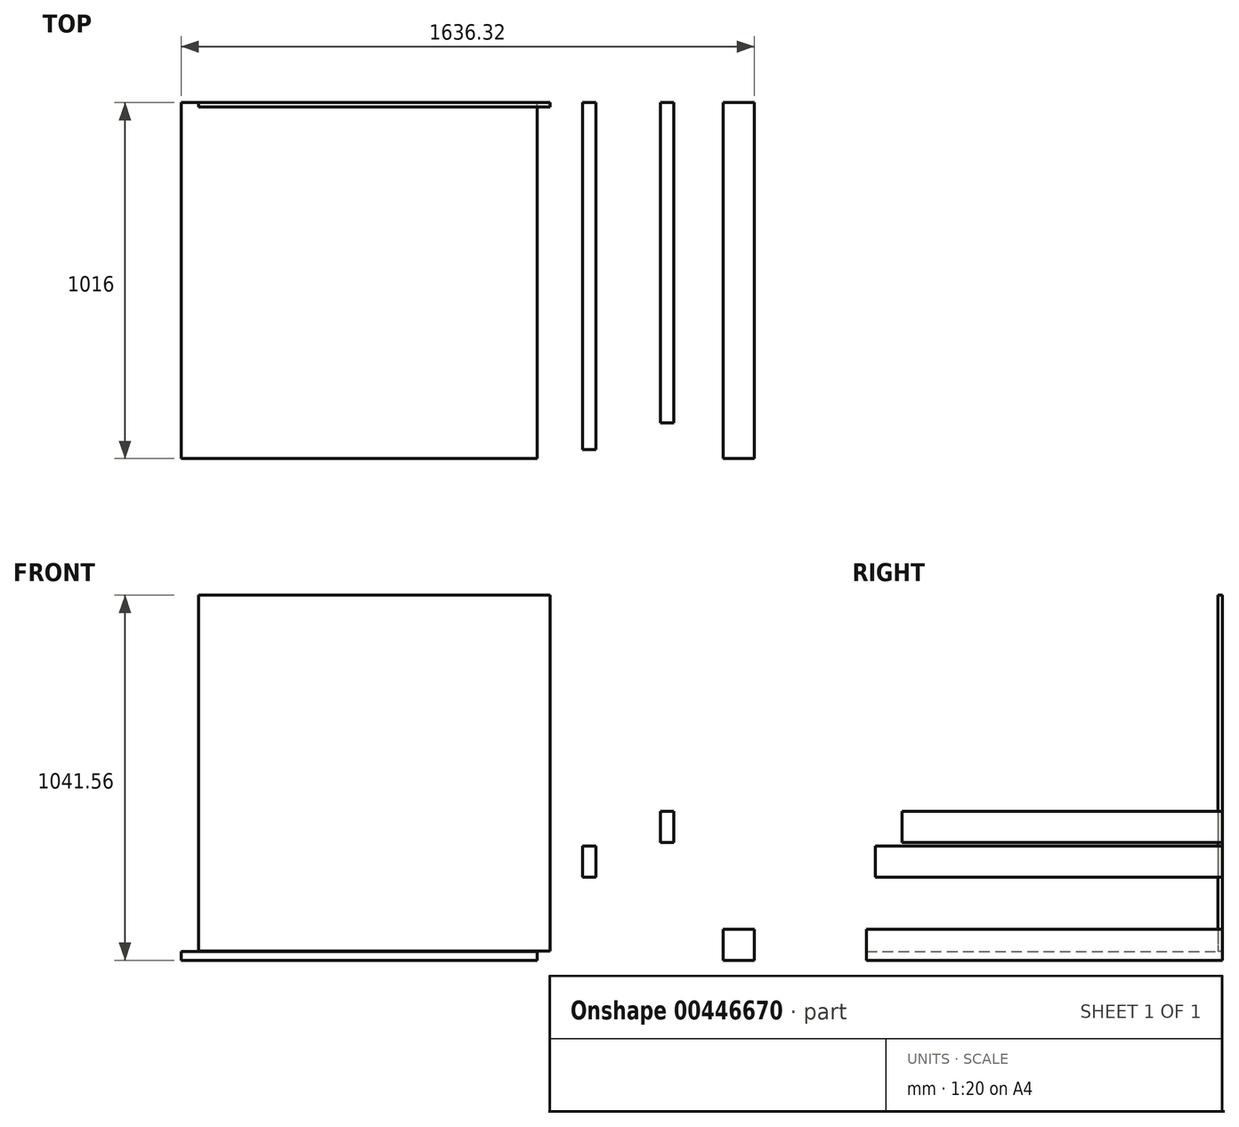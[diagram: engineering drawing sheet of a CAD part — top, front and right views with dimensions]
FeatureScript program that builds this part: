
annotation { "Feature Type Name" : "Feature", "Feature Type Description" : "" }
export const myFeature = defineFeature(function(context is Context, id is Id, definition is map)
    precondition{}
    {
        {
            var Q0;
            Q0=qCreatedBy(makeId("Front.planeOp"),FACE);
            var sketch = newSketch(context, id + "F0", { "sketchPlane" : qUnion([Q0])});
            skLineSegment(sketch, "E0.bottom", {"start": v(0, 0) * mm, "end": v(88.9, 0) * mm});
            skLineSegment(sketch, "E0.top", {"start": v(0, 88.9) * mm, "end": v(88.9, 88.9) * mm});
            skLineSegment(sketch, "E0.left", {"start": v(0, 0) * mm, "end": v(0, 88.9) * mm});
            skLineSegment(sketch, "E0.right", {"start": v(88.9, 0) * mm, "end": v(88.9, 88.9) * mm});
            skSolve(sketch);
        }
        {
            var Q0;
            Q0=makeQuery(id+"F0.imprint","IMPRINT",FACE,{"disambiguationData":[TD([[makeQuery(id+"F0.imprint","IMPRINT",EDGE,{"derivedFrom":sQuery(id+"F0.wireOp",EDGE,"E0.bottom")}),1.0]])]});
            extrude(context, id + "F1", {"entities" : qUnion([Q0]), "depth" : 1016 * mm, "offsetDistance" : 25.4 * mm});
        }
        {
            var Q0;
            Q0=qCreatedBy(makeId("Top.planeOp"),FACE);
            var sketch = newSketch(context, id + "F2", { "sketchPlane" : qUnion([Q0])});
            skLineSegment(sketch, "E1.bottom", {"start": v(-531.42, -1016) * mm, "end": v(-1547.42, -1016) * mm});
            skLineSegment(sketch, "E1.top", {"start": v(-531.42, 0) * mm, "end": v(-1547.42, 0) * mm});
            skLineSegment(sketch, "E1.left", {"start": v(-531.42, -1016) * mm, "end": v(-531.42, 0) * mm});
            skLineSegment(sketch, "E1.right", {"start": v(-1547.42, -1016) * mm, "end": v(-1547.42, 0) * mm});
            skSolve(sketch);
        }
        {
            var Q0;
            Q0=makeQuery(id+"F2.imprint","IMPRINT",FACE,{"disambiguationData":[TD([[makeQuery(id+"F2.imprint","IMPRINT",EDGE,{"derivedFrom":sQuery(id+"F2.wireOp",EDGE,"E1.bottom")}),-1.0]])]});
            extrude(context, id + "F3", {"entities" : qUnion([Q0]), "depth" : 25.4 * mm, "offsetDistance" : 25.4 * mm});
        }
        {
            var Q0;
            Q0=qCreatedBy(makeId("Front.planeOp"),FACE);
            var sketch = newSketch(context, id + "F4", { "sketchPlane" : qUnion([Q0])});
            skLineSegment(sketch, "E2.bottom", {"start": v(-401.15, 236.5) * mm, "end": v(-363.05, 236.5) * mm});
            skLineSegment(sketch, "E2.top", {"start": v(-401.15, 325.4) * mm, "end": v(-363.05, 325.4) * mm});
            skLineSegment(sketch, "E2.left", {"start": v(-401.15, 236.5) * mm, "end": v(-401.15, 325.4) * mm});
            skLineSegment(sketch, "E2.right", {"start": v(-363.05, 236.5) * mm, "end": v(-363.05, 325.4) * mm});
            skSolve(sketch);
        }
        {
            var Q0;
            Q0=makeQuery(id+"F4.imprint","IMPRINT",FACE,{"disambiguationData":[TD([[makeQuery(id+"F4.imprint","IMPRINT",EDGE,{"derivedFrom":sQuery(id+"F4.wireOp",EDGE,"E2.bottom")}),1.0]])]});
            extrude(context, id + "F5", {"entities" : qUnion([Q0]), "depth" : 990.6 * mm, "offsetDistance" : 25.4 * mm});
        }
        {
            var Q0;
            Q0=qCreatedBy(makeId("Front.planeOp"),FACE);
            var sketch = newSketch(context, id + "F6", { "sketchPlane" : qUnion([Q0])});
            skLineSegment(sketch, "E3.bottom", {"start": v(-1496.68, 1041.56) * mm, "end": v(-493.38, 1041.56) * mm});
            skLineSegment(sketch, "E3.top", {"start": v(-1496.68, 25.56) * mm, "end": v(-493.38, 25.56) * mm});
            skLineSegment(sketch, "E3.left", {"start": v(-1496.68, 1041.56) * mm, "end": v(-1496.68, 25.56) * mm});
            skLineSegment(sketch, "E3.right", {"start": v(-493.38, 1041.56) * mm, "end": v(-493.38, 25.56) * mm});
            skSolve(sketch);
        }
        {
            var Q0;
            Q0=makeQuery(id+"F6.imprint","IMPRINT",FACE,{"disambiguationData":[TD([[makeQuery(id+"F6.imprint","IMPRINT",EDGE,{"derivedFrom":sQuery(id+"F6.wireOp",EDGE,"E3.bottom")}),-1.0]])]});
            extrude(context, id + "F7", {"entities" : qUnion([Q0]), "depth" : 12.7 * mm, "offsetDistance" : 25.4 * mm});
        }
        {
            var Q0;
            Q0=qCreatedBy(makeId("Front.planeOp"),FACE);
            var sketch = newSketch(context, id + "F8", { "sketchPlane" : qUnion([Q0])});
            skLineSegment(sketch, "E4.bottom", {"start": v(-178.49, 335.67) * mm, "end": v(-140.39, 335.67) * mm});
            skLineSegment(sketch, "E4.top", {"start": v(-178.49, 424.57) * mm, "end": v(-140.39, 424.57) * mm});
            skLineSegment(sketch, "E4.left", {"start": v(-178.49, 335.67) * mm, "end": v(-178.49, 424.57) * mm});
            skLineSegment(sketch, "E4.right", {"start": v(-140.39, 335.67) * mm, "end": v(-140.39, 424.57) * mm});
            skSolve(sketch);
        }
        {
            var Q0;
            Q0=makeQuery(id+"F8.imprint","IMPRINT",FACE,{"disambiguationData":[TD([[makeQuery(id+"F8.imprint","IMPRINT",EDGE,{"derivedFrom":sQuery(id+"F8.wireOp",EDGE,"E4.bottom")}),1.0]])]});
            extrude(context, id + "F9", {"entities" : qUnion([Q0]), "depth" : 914.4 * mm, "offsetDistance" : 25.4 * mm});
        }
    });
